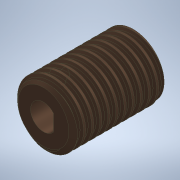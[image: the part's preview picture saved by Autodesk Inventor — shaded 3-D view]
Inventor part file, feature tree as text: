
AUTODESK INVENTOR PART (.ipt)
format: ipt  version: 2022 (Build 260153000, 153)  size: 1,351,680 bytes
history: imported  units: in
note: dims shown in document units (in); Inventor stores cm internally (conversion verified against a paired STEP export)
features: imported_body x1
ambient origin geometry x8: Origin, YZ Plane, XZ Plane, XY Plane, X Axis, Y Axis, Z Axis, Center Point
bodies: Solid1 (imported_parasolid), Body3 (imported_parasolid)
feature tree (1):
  imported_body  NMx_Import_Brep_tag  [imported B-rep: ~4 faces, bbox_mm=None]
